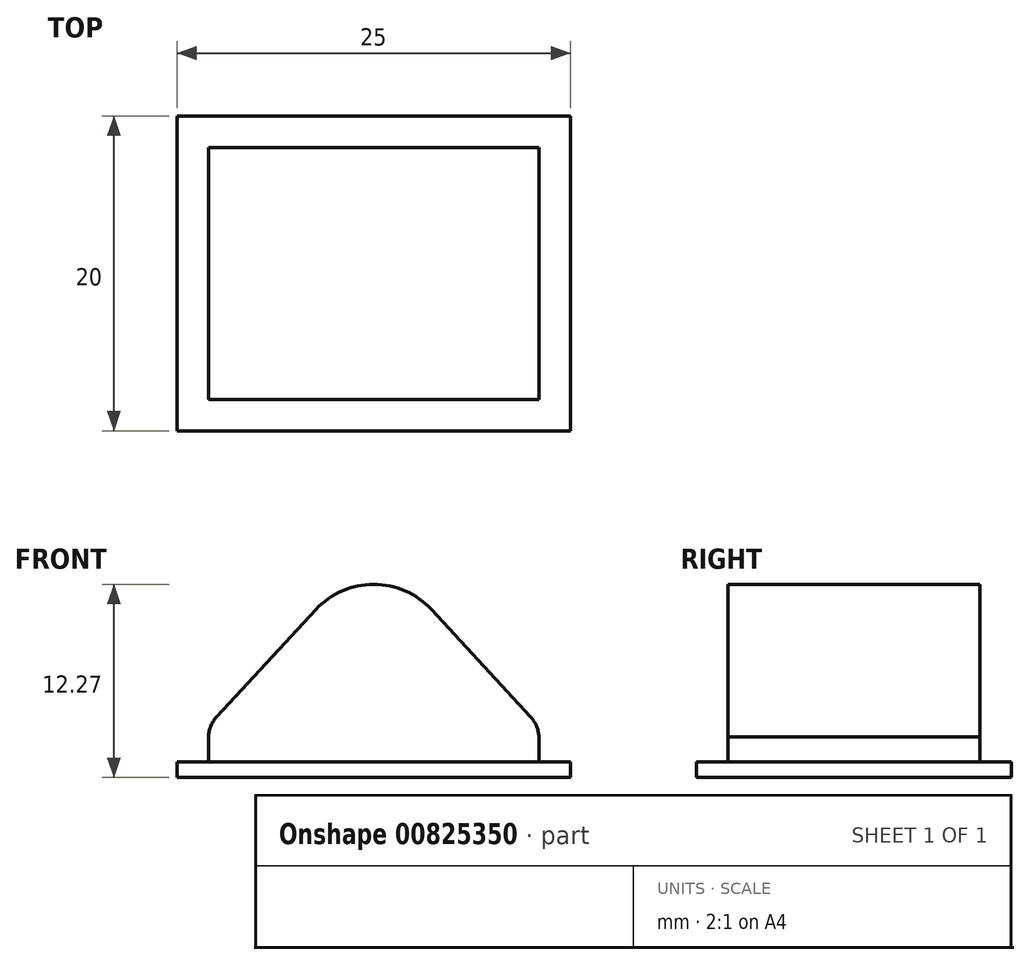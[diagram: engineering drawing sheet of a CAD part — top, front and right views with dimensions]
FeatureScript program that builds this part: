
annotation { "Feature Type Name" : "Feature", "Feature Type Description" : "" }
export const myFeature = defineFeature(function(context is Context, id is Id, definition is map)
    precondition{}
    {
        {
            var Q0;
            Q0=qCreatedBy(makeId("Top.planeOp"),FACE);
            var sketch = newSketch(context, id + "F0", { "sketchPlane" : qUnion([Q0])});
            skLineSegment(sketch, "E0.bottom", {"start": v(12.5, -10) * mm, "end": v(-12.5, -10) * mm});
            skLineSegment(sketch, "E0.top", {"start": v(12.5, 10) * mm, "end": v(-12.5, 10) * mm});
            skLineSegment(sketch, "E0.left", {"start": v(12.5, -10) * mm, "end": v(12.5, 10) * mm});
            skLineSegment(sketch, "E0.right", {"start": v(-12.5, -10) * mm, "end": v(-12.5, 10) * mm});
            skPoint(sketch, "E0.middle", {"position": v(0, 0) * mm});
            skPoint(sketch, "E1.top.end.orphan", {"position": v(-10.5, 8) * mm});
            skPoint(sketch, "E1.left.end.orphan", {"position": v(10.5, 8) * mm});
            skPoint(sketch, "E1.bottom.end.orphan", {"position": v(-10.5, -8) * mm});
            skPoint(sketch, "E1.bottom.start.orphan", {"position": v(10.5, -8) * mm});
            skSolve(sketch);
        }
        {
            var Q0;
            Q0=makeQuery(id+"F0.imprint","IMPRINT",FACE,{"disambiguationData":[TD([[makeQuery(id+"F0.imprint","IMPRINT",EDGE,{"derivedFrom":sQuery(id+"F0.wireOp",EDGE,"E0.bottom")}),-1.0]])]});
            extrude(context, id + "F1", {"entities" : qUnion([Q0]), "depth" : 1 * mm, "offsetDistance" : 25 * mm});
        }
        {
            var Q0;
            Q0=qCreatedBy(makeId("Front.planeOp"),FACE);
            var sketch = newSketch(context, id + "F2", { "sketchPlane" : qUnion([Q0])});
            skArc(sketch, "E2", {"start": v(3.67, 10.67) * mm, "mid": v(0, 12.27) * mm, "end": v(-3.67, 10.67) * mm});
            skLineSegment(sketch, "E3.bottom", {"start": v(8.5, 2.5) * mm, "end": v(-8.5, 2.5) * mm, "construction": true});
            skLineSegment(sketch, "E3.top", {"start": v(8.5, -2.5) * mm, "end": v(-8.5, -2.5) * mm, "construction": true});
            skLineSegment(sketch, "E3.left", {"start": v(8.5, 2.5) * mm, "end": v(8.5, -2.5) * mm, "construction": true});
            skLineSegment(sketch, "E3.right", {"start": v(-8.5, 2.5) * mm, "end": v(-8.5, -2.5) * mm, "construction": true});
            skPoint(sketch, "E3.middle", {"position": v(0, 0) * mm});
            skArc(sketch, "E4", {"start": v(-9.97, 3.86) * mm, "mid": v(-10.36, 3.23) * mm, "end": v(-10.5, 2.5) * mm});
            skArc(sketch, "E5", {"start": v(10.5, 2.42) * mm, "mid": v(10.38, 3.19) * mm, "end": v(9.97, 3.86) * mm});
            skLineSegment(sketch, "E6", {"start": v(-10.5, 2.5) * mm, "end": v(-10.5, 0) * mm});
            skLineSegment(sketch, "E7", {"start": v(10.5, 2.58) * mm, "end": v(10.5, 0) * mm});
            skLineSegment(sketch, "E8", {"start": v(10.5, 0) * mm, "end": v(-10.5, 0) * mm});
            skLineSegment(sketch, "E9", {"start": v(-9.97, 3.86) * mm, "end": v(-3.67, 10.67) * mm});
            skLineSegment(sketch, "E10", {"start": v(3.67, 10.67) * mm, "end": v(9.97, 3.86) * mm});
            skSolve(sketch);
        }
        {
            var Q0;
            Q0=makeQuery(id+"F2.imprint","IMPRINT",FACE,{"disambiguationData":[TD([[makeQuery(id+"F2.imprint","IMPRINT",EDGE,{"derivedFrom":sQuery(id+"F2.wireOp",EDGE,"E2")}),1.0]])]});
            extrude(context, id + "F3", {"entities" : qUnion([Q0]), "operationType" : NewBodyOperationType.ADD, "endBound" : BoundingType.SYMMETRIC, "depth" : 16 * mm, "offsetDistance" : 25 * mm});
        }
    });
